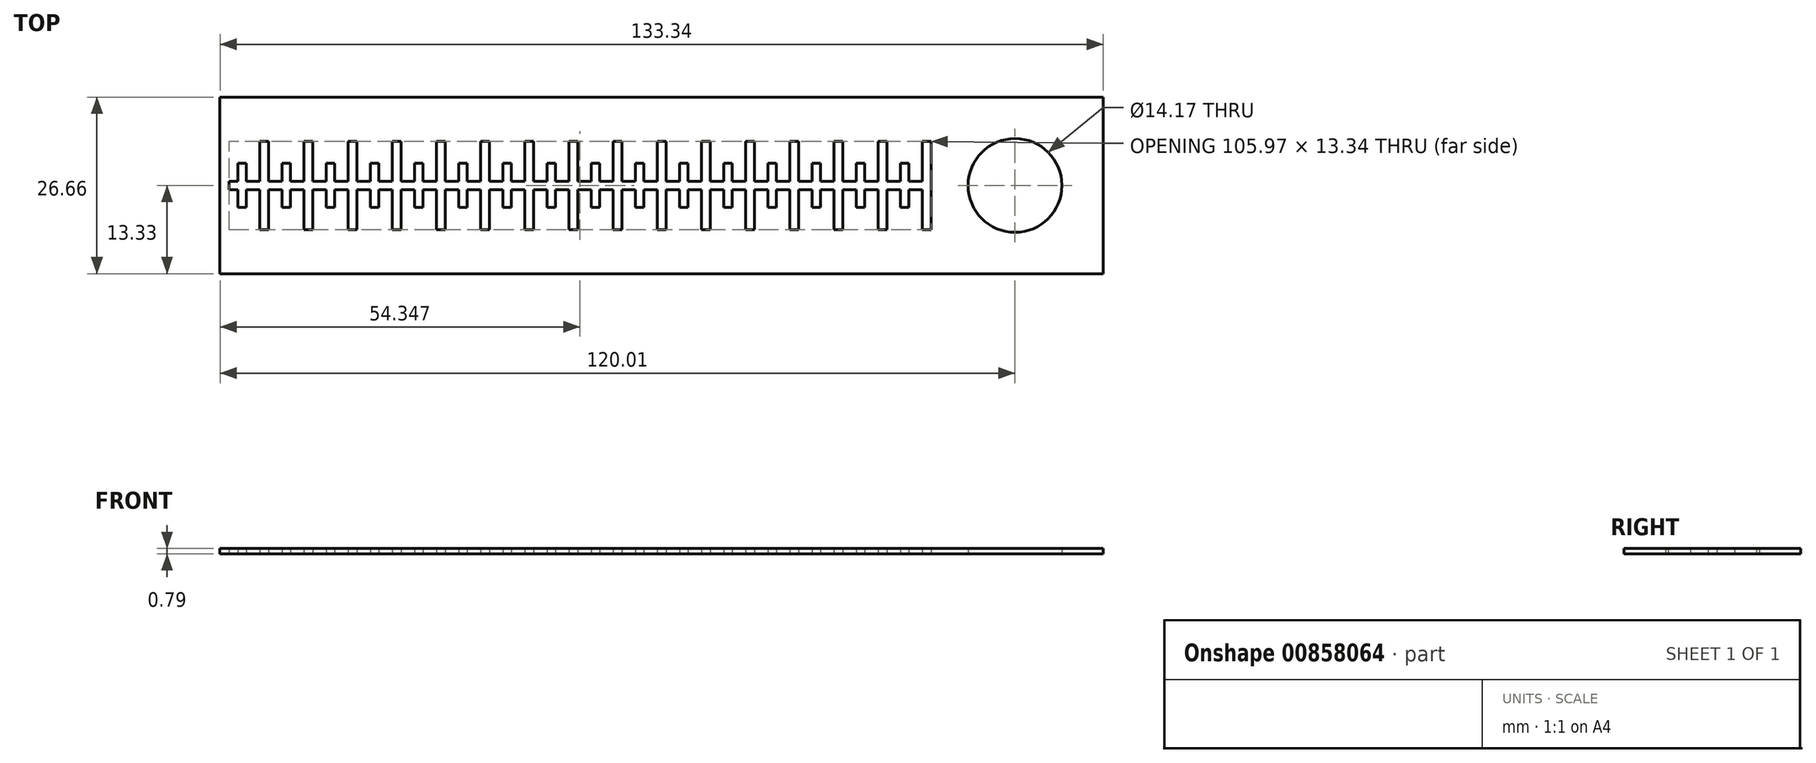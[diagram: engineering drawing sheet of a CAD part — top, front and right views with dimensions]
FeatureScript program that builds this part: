
annotation { "Feature Type Name" : "Feature", "Feature Type Description" : "" }
export const myFeature = defineFeature(function(context is Context, id is Id, definition is map)
    precondition{}
    {
        {
            var Q0;
            Q0=qCreatedBy(makeId("Top.planeOp"),FACE);
            var sketch = newSketch(context, id + "F0", { "sketchPlane" : qUnion([Q0])});
            skLineSegment(sketch, "E0.bottom", {"start": v(63.5, -12.7) * mm, "end": v(-63.5, -12.7) * mm});
            skLineSegment(sketch, "E0.top", {"start": v(63.5, 12.7) * mm, "end": v(-63.5, 12.7) * mm});
            skLineSegment(sketch, "E0.left", {"start": v(63.5, -12.7) * mm, "end": v(63.5, 12.7) * mm});
            skLineSegment(sketch, "E0.right", {"start": v(-63.5, -12.7) * mm, "end": v(-63.5, 12.7) * mm});
            skPoint(sketch, "E1", {"position": v(-60.33, 0) * mm});
            skPoint(sketch, "E2", {"position": v(-57.15, 0) * mm});
            skLineSegment(sketch, "E3.bottom", {"start": v(-57.15, -0.62) * mm, "end": v(-63.5, -0.62) * mm});
            skLineSegment(sketch, "E3.top", {"start": v(-57.15, 0.62) * mm, "end": v(-63.5, 0.62) * mm});
            skLineSegment(sketch, "E3.left", {"start": v(-57.15, -0.62) * mm, "end": v(-57.15, 0.62) * mm});
            skLineSegment(sketch, "E3.right", {"start": v(-63.5, -0.62) * mm, "end": v(-63.5, 0.62) * mm});
            skLineSegment(sketch, "E4.bottom", {"start": v(-59.7, -3.18) * mm, "end": v(-60.95, -3.18) * mm});
            skLineSegment(sketch, "E4.top", {"start": v(-59.7, 3.17) * mm, "end": v(-60.95, 3.17) * mm});
            skLineSegment(sketch, "E4.left", {"start": v(-59.7, -3.18) * mm, "end": v(-59.7, 3.17) * mm});
            skLineSegment(sketch, "E4.right", {"start": v(-60.95, -3.18) * mm, "end": v(-60.95, 3.17) * mm});
            skLineSegment(sketch, "E5.bottom", {"start": v(-56.52, -6.35) * mm, "end": v(-57.77, -6.35) * mm});
            skLineSegment(sketch, "E5.top", {"start": v(-56.52, 6.35) * mm, "end": v(-57.77, 6.35) * mm});
            skLineSegment(sketch, "E5.left", {"start": v(-56.52, -6.35) * mm, "end": v(-56.52, 6.35) * mm});
            skLineSegment(sketch, "E5.right", {"start": v(-57.77, -6.35) * mm, "end": v(-57.77, 6.35) * mm});
            skPoint(sketch, "E6.1.0.0", {"position": v(-50.8, 0) * mm});
            skLineSegment(sketch, "E6.1.0.1", {"start": v(-54.6, -3.18) * mm, "end": v(-54.6, 3.17) * mm});
            skLineSegment(sketch, "E6.1.0.2", {"start": v(-50.17, -6.35) * mm, "end": v(-50.17, 6.35) * mm});
            skPoint(sketch, "E6.1.0.3", {"position": v(-53.98, 0) * mm});
            skLineSegment(sketch, "E6.1.0.4", {"start": v(-53.35, -3.18) * mm, "end": v(-53.35, 3.17) * mm});
            skLineSegment(sketch, "E6.1.0.5", {"start": v(-51.42, -6.35) * mm, "end": v(-51.42, 6.35) * mm});
            skLineSegment(sketch, "E6.1.0.6", {"start": v(-50.8, 0.62) * mm, "end": v(-57.15, 0.62) * mm});
            skLineSegment(sketch, "E6.1.0.7", {"start": v(-50.8, -0.62) * mm, "end": v(-57.15, -0.62) * mm});
            skPoint(sketch, "E6.1.0.8", {"position": v(-50.8, 0) * mm});
            skPoint(sketch, "E6.1.0.9", {"position": v(-53.98, 0) * mm});
            skLineSegment(sketch, "E6.1.0.11", {"start": v(-50.8, -0.62) * mm, "end": v(-50.8, 0.62) * mm});
            skLineSegment(sketch, "E6.1.0.12", {"start": v(-53.35, -3.18) * mm, "end": v(-54.6, -3.18) * mm});
            skLineSegment(sketch, "E6.1.0.13", {"start": v(-53.35, 3.17) * mm, "end": v(-54.6, 3.17) * mm});
            skLineSegment(sketch, "E6.1.0.14", {"start": v(-50.17, -6.35) * mm, "end": v(-51.42, -6.35) * mm});
            skLineSegment(sketch, "E6.1.0.15", {"start": v(-50.17, 6.35) * mm, "end": v(-51.42, 6.35) * mm});
            skPoint(sketch, "E6.1.0.16", {"position": v(-53.98, 0) * mm});
            skPoint(sketch, "E6.2.0.0", {"position": v(-44.45, 0) * mm});
            skLineSegment(sketch, "E6.2.0.1", {"start": v(-48.25, -3.18) * mm, "end": v(-48.25, 3.17) * mm});
            skLineSegment(sketch, "E6.2.0.2", {"start": v(-43.82, -6.35) * mm, "end": v(-43.82, 6.35) * mm});
            skPoint(sketch, "E6.2.0.3", {"position": v(-47.62, 0) * mm});
            skLineSegment(sketch, "E6.2.0.4", {"start": v(-47, -3.18) * mm, "end": v(-47, 3.17) * mm});
            skLineSegment(sketch, "E6.2.0.5", {"start": v(-45.07, -6.35) * mm, "end": v(-45.07, 6.35) * mm});
            skLineSegment(sketch, "E6.2.0.6", {"start": v(-44.45, 0.62) * mm, "end": v(-50.8, 0.62) * mm});
            skLineSegment(sketch, "E6.2.0.7", {"start": v(-44.45, -0.62) * mm, "end": v(-50.8, -0.62) * mm});
            skPoint(sketch, "E6.2.0.8", {"position": v(-44.45, 0) * mm});
            skPoint(sketch, "E6.2.0.9", {"position": v(-47.62, 0) * mm});
            skLineSegment(sketch, "E6.2.0.10", {"start": v(-50.8, -0.62) * mm, "end": v(-50.8, 0.62) * mm});
            skLineSegment(sketch, "E6.2.0.11", {"start": v(-44.45, -0.62) * mm, "end": v(-44.45, 0.62) * mm});
            skLineSegment(sketch, "E6.2.0.12", {"start": v(-47, -3.18) * mm, "end": v(-48.25, -3.18) * mm});
            skLineSegment(sketch, "E6.2.0.13", {"start": v(-47, 3.17) * mm, "end": v(-48.25, 3.17) * mm});
            skLineSegment(sketch, "E6.2.0.14", {"start": v(-43.82, -6.35) * mm, "end": v(-45.07, -6.35) * mm});
            skLineSegment(sketch, "E6.2.0.15", {"start": v(-43.82, 6.35) * mm, "end": v(-45.07, 6.35) * mm});
            skPoint(sketch, "E6.2.0.16", {"position": v(-47.62, 0) * mm});
            skPoint(sketch, "E6.3.0.0", {"position": v(-38.1, 0) * mm});
            skLineSegment(sketch, "E6.3.0.1", {"start": v(-41.9, -3.18) * mm, "end": v(-41.9, 3.17) * mm});
            skLineSegment(sketch, "E6.3.0.2", {"start": v(-37.47, -6.35) * mm, "end": v(-37.47, 6.35) * mm});
            skPoint(sketch, "E6.3.0.3", {"position": v(-41.27, 0) * mm});
            skLineSegment(sketch, "E6.3.0.4", {"start": v(-40.65, -3.18) * mm, "end": v(-40.65, 3.17) * mm});
            skLineSegment(sketch, "E6.3.0.5", {"start": v(-38.72, -6.35) * mm, "end": v(-38.72, 6.35) * mm});
            skLineSegment(sketch, "E6.3.0.6", {"start": v(-38.1, 0.62) * mm, "end": v(-44.45, 0.62) * mm});
            skLineSegment(sketch, "E6.3.0.7", {"start": v(-38.1, -0.62) * mm, "end": v(-44.45, -0.62) * mm});
            skPoint(sketch, "E6.3.0.8", {"position": v(-38.1, 0) * mm});
            skPoint(sketch, "E6.3.0.9", {"position": v(-41.27, 0) * mm});
            skLineSegment(sketch, "E6.3.0.10", {"start": v(-44.45, -0.62) * mm, "end": v(-44.45, 0.62) * mm});
            skLineSegment(sketch, "E6.3.0.11", {"start": v(-38.1, -0.62) * mm, "end": v(-38.1, 0.62) * mm});
            skLineSegment(sketch, "E6.3.0.12", {"start": v(-40.65, -3.18) * mm, "end": v(-41.9, -3.18) * mm});
            skLineSegment(sketch, "E6.3.0.13", {"start": v(-40.65, 3.17) * mm, "end": v(-41.9, 3.17) * mm});
            skLineSegment(sketch, "E6.3.0.14", {"start": v(-37.47, -6.35) * mm, "end": v(-38.72, -6.35) * mm});
            skLineSegment(sketch, "E6.3.0.15", {"start": v(-37.47, 6.35) * mm, "end": v(-38.72, 6.35) * mm});
            skPoint(sketch, "E6.3.0.16", {"position": v(-41.27, 0) * mm});
            skPoint(sketch, "E6.4.0.0", {"position": v(-31.75, 0) * mm});
            skLineSegment(sketch, "E6.4.0.1", {"start": v(-35.55, -3.18) * mm, "end": v(-35.55, 3.17) * mm});
            skLineSegment(sketch, "E6.4.0.2", {"start": v(-31.12, -6.35) * mm, "end": v(-31.12, 6.35) * mm});
            skPoint(sketch, "E6.4.0.3", {"position": v(-34.92, 0) * mm});
            skLineSegment(sketch, "E6.4.0.4", {"start": v(-34.3, -3.18) * mm, "end": v(-34.3, 3.17) * mm});
            skLineSegment(sketch, "E6.4.0.5", {"start": v(-32.37, -6.35) * mm, "end": v(-32.37, 6.35) * mm});
            skLineSegment(sketch, "E6.4.0.6", {"start": v(-31.75, 0.62) * mm, "end": v(-38.1, 0.62) * mm});
            skLineSegment(sketch, "E6.4.0.7", {"start": v(-31.75, -0.62) * mm, "end": v(-38.1, -0.62) * mm});
            skPoint(sketch, "E6.4.0.8", {"position": v(-31.75, 0) * mm});
            skPoint(sketch, "E6.4.0.9", {"position": v(-34.92, 0) * mm});
            skLineSegment(sketch, "E6.4.0.10", {"start": v(-38.1, -0.62) * mm, "end": v(-38.1, 0.62) * mm});
            skLineSegment(sketch, "E6.4.0.11", {"start": v(-31.75, -0.62) * mm, "end": v(-31.75, 0.62) * mm});
            skLineSegment(sketch, "E6.4.0.12", {"start": v(-34.3, -3.18) * mm, "end": v(-35.55, -3.18) * mm});
            skLineSegment(sketch, "E6.4.0.13", {"start": v(-34.3, 3.17) * mm, "end": v(-35.55, 3.17) * mm});
            skLineSegment(sketch, "E6.4.0.14", {"start": v(-31.12, -6.35) * mm, "end": v(-32.37, -6.35) * mm});
            skLineSegment(sketch, "E6.4.0.15", {"start": v(-31.12, 6.35) * mm, "end": v(-32.37, 6.35) * mm});
            skPoint(sketch, "E6.4.0.16", {"position": v(-34.92, 0) * mm});
            skPoint(sketch, "E6.5.0.0", {"position": v(-25.4, 0) * mm});
            skLineSegment(sketch, "E6.5.0.1", {"start": v(-29.2, -3.18) * mm, "end": v(-29.2, 3.17) * mm});
            skLineSegment(sketch, "E6.5.0.2", {"start": v(-24.77, -6.35) * mm, "end": v(-24.77, 6.35) * mm});
            skPoint(sketch, "E6.5.0.3", {"position": v(-28.57, 0) * mm});
            skLineSegment(sketch, "E6.5.0.4", {"start": v(-27.95, -3.18) * mm, "end": v(-27.95, 3.17) * mm});
            skLineSegment(sketch, "E6.5.0.5", {"start": v(-26.02, -6.35) * mm, "end": v(-26.02, 6.35) * mm});
            skLineSegment(sketch, "E6.5.0.6", {"start": v(-25.4, 0.62) * mm, "end": v(-31.75, 0.62) * mm});
            skLineSegment(sketch, "E6.5.0.7", {"start": v(-25.4, -0.62) * mm, "end": v(-31.75, -0.62) * mm});
            skPoint(sketch, "E6.5.0.8", {"position": v(-25.4, 0) * mm});
            skPoint(sketch, "E6.5.0.9", {"position": v(-28.57, 0) * mm});
            skLineSegment(sketch, "E6.5.0.10", {"start": v(-31.75, -0.62) * mm, "end": v(-31.75, 0.62) * mm});
            skLineSegment(sketch, "E6.5.0.11", {"start": v(-25.4, -0.62) * mm, "end": v(-25.4, 0.62) * mm});
            skLineSegment(sketch, "E6.5.0.12", {"start": v(-27.95, -3.18) * mm, "end": v(-29.2, -3.18) * mm});
            skLineSegment(sketch, "E6.5.0.13", {"start": v(-27.95, 3.17) * mm, "end": v(-29.2, 3.17) * mm});
            skLineSegment(sketch, "E6.5.0.14", {"start": v(-24.77, -6.35) * mm, "end": v(-26.02, -6.35) * mm});
            skLineSegment(sketch, "E6.5.0.15", {"start": v(-24.77, 6.35) * mm, "end": v(-26.02, 6.35) * mm});
            skPoint(sketch, "E6.5.0.16", {"position": v(-28.57, 0) * mm});
            skPoint(sketch, "E6.6.0.0", {"position": v(-19.05, 0) * mm});
            skLineSegment(sketch, "E6.6.0.1", {"start": v(-22.85, -3.18) * mm, "end": v(-22.85, 3.17) * mm});
            skLineSegment(sketch, "E6.6.0.2", {"start": v(-18.42, -6.35) * mm, "end": v(-18.42, 6.35) * mm});
            skPoint(sketch, "E6.6.0.3", {"position": v(-22.22, 0) * mm});
            skLineSegment(sketch, "E6.6.0.4", {"start": v(-21.6, -3.18) * mm, "end": v(-21.6, 3.17) * mm});
            skLineSegment(sketch, "E6.6.0.5", {"start": v(-19.67, -6.35) * mm, "end": v(-19.67, 6.35) * mm});
            skLineSegment(sketch, "E6.6.0.6", {"start": v(-19.05, 0.62) * mm, "end": v(-25.4, 0.62) * mm});
            skLineSegment(sketch, "E6.6.0.7", {"start": v(-19.05, -0.62) * mm, "end": v(-25.4, -0.62) * mm});
            skPoint(sketch, "E6.6.0.8", {"position": v(-19.05, 0) * mm});
            skPoint(sketch, "E6.6.0.9", {"position": v(-22.22, 0) * mm});
            skLineSegment(sketch, "E6.6.0.10", {"start": v(-25.4, -0.62) * mm, "end": v(-25.4, 0.62) * mm});
            skLineSegment(sketch, "E6.6.0.11", {"start": v(-19.05, -0.62) * mm, "end": v(-19.05, 0.62) * mm});
            skLineSegment(sketch, "E6.6.0.12", {"start": v(-21.6, -3.18) * mm, "end": v(-22.85, -3.18) * mm});
            skLineSegment(sketch, "E6.6.0.13", {"start": v(-21.6, 3.17) * mm, "end": v(-22.85, 3.17) * mm});
            skLineSegment(sketch, "E6.6.0.14", {"start": v(-18.42, -6.35) * mm, "end": v(-19.67, -6.35) * mm});
            skLineSegment(sketch, "E6.6.0.15", {"start": v(-18.42, 6.35) * mm, "end": v(-19.67, 6.35) * mm});
            skPoint(sketch, "E6.6.0.16", {"position": v(-22.22, 0) * mm});
            skPoint(sketch, "E6.7.0.0", {"position": v(-12.7, 0) * mm});
            skLineSegment(sketch, "E6.7.0.1", {"start": v(-16.5, -3.18) * mm, "end": v(-16.5, 3.17) * mm});
            skLineSegment(sketch, "E6.7.0.2", {"start": v(-12.07, -6.35) * mm, "end": v(-12.07, 6.35) * mm});
            skPoint(sketch, "E6.7.0.3", {"position": v(-15.87, 0) * mm});
            skLineSegment(sketch, "E6.7.0.4", {"start": v(-15.25, -3.18) * mm, "end": v(-15.25, 3.17) * mm});
            skLineSegment(sketch, "E6.7.0.5", {"start": v(-13.32, -6.35) * mm, "end": v(-13.32, 6.35) * mm});
            skLineSegment(sketch, "E6.7.0.6", {"start": v(-12.7, 0.62) * mm, "end": v(-19.05, 0.62) * mm});
            skLineSegment(sketch, "E6.7.0.7", {"start": v(-12.7, -0.62) * mm, "end": v(-19.05, -0.62) * mm});
            skPoint(sketch, "E6.7.0.8", {"position": v(-12.7, 0) * mm});
            skPoint(sketch, "E6.7.0.9", {"position": v(-15.87, 0) * mm});
            skLineSegment(sketch, "E6.7.0.10", {"start": v(-19.05, -0.62) * mm, "end": v(-19.05, 0.62) * mm});
            skLineSegment(sketch, "E6.7.0.11", {"start": v(-12.7, -0.62) * mm, "end": v(-12.7, 0.62) * mm});
            skLineSegment(sketch, "E6.7.0.12", {"start": v(-15.25, -3.18) * mm, "end": v(-16.5, -3.18) * mm});
            skLineSegment(sketch, "E6.7.0.13", {"start": v(-15.25, 3.17) * mm, "end": v(-16.5, 3.17) * mm});
            skLineSegment(sketch, "E6.7.0.14", {"start": v(-12.07, -6.35) * mm, "end": v(-13.32, -6.35) * mm});
            skLineSegment(sketch, "E6.7.0.15", {"start": v(-12.07, 6.35) * mm, "end": v(-13.32, 6.35) * mm});
            skPoint(sketch, "E6.7.0.16", {"position": v(-15.87, 0) * mm});
            skPoint(sketch, "E6.8.0.0", {"position": v(-6.35, 0) * mm});
            skLineSegment(sketch, "E6.8.0.1", {"start": v(-10.15, -3.18) * mm, "end": v(-10.15, 3.17) * mm});
            skLineSegment(sketch, "E6.8.0.2", {"start": v(-5.72, -6.35) * mm, "end": v(-5.72, 6.35) * mm});
            skPoint(sketch, "E6.8.0.3", {"position": v(-9.52, 0) * mm});
            skLineSegment(sketch, "E6.8.0.4", {"start": v(-8.9, -3.18) * mm, "end": v(-8.9, 3.17) * mm});
            skLineSegment(sketch, "E6.8.0.5", {"start": v(-6.97, -6.35) * mm, "end": v(-6.97, 6.35) * mm});
            skLineSegment(sketch, "E6.8.0.6", {"start": v(-6.35, 0.62) * mm, "end": v(-12.7, 0.62) * mm});
            skLineSegment(sketch, "E6.8.0.7", {"start": v(-6.35, -0.62) * mm, "end": v(-12.7, -0.62) * mm});
            skPoint(sketch, "E6.8.0.8", {"position": v(-6.35, 0) * mm});
            skPoint(sketch, "E6.8.0.9", {"position": v(-9.52, 0) * mm});
            skLineSegment(sketch, "E6.8.0.10", {"start": v(-12.7, -0.62) * mm, "end": v(-12.7, 0.62) * mm});
            skLineSegment(sketch, "E6.8.0.11", {"start": v(-6.35, -0.62) * mm, "end": v(-6.35, 0.62) * mm});
            skLineSegment(sketch, "E6.8.0.12", {"start": v(-8.9, -3.18) * mm, "end": v(-10.15, -3.18) * mm});
            skLineSegment(sketch, "E6.8.0.13", {"start": v(-8.9, 3.17) * mm, "end": v(-10.15, 3.17) * mm});
            skLineSegment(sketch, "E6.8.0.14", {"start": v(-5.72, -6.35) * mm, "end": v(-6.97, -6.35) * mm});
            skLineSegment(sketch, "E6.8.0.15", {"start": v(-5.72, 6.35) * mm, "end": v(-6.97, 6.35) * mm});
            skPoint(sketch, "E6.8.0.16", {"position": v(-9.52, 0) * mm});
            skPoint(sketch, "E6.9.0.0", {"position": v(0, 0) * mm});
            skLineSegment(sketch, "E6.9.0.1", {"start": v(-3.8, -3.18) * mm, "end": v(-3.8, 3.17) * mm});
            skLineSegment(sketch, "E6.9.0.2", {"start": v(0.63, -6.35) * mm, "end": v(0.63, 6.35) * mm});
            skPoint(sketch, "E6.9.0.3", {"position": v(-3.17, 0) * mm});
            skLineSegment(sketch, "E6.9.0.4", {"start": v(-2.55, -3.18) * mm, "end": v(-2.55, 3.17) * mm});
            skLineSegment(sketch, "E6.9.0.5", {"start": v(-0.62, -6.35) * mm, "end": v(-0.62, 6.35) * mm});
            skLineSegment(sketch, "E6.9.0.6", {"start": v(0, 0.62) * mm, "end": v(-6.35, 0.62) * mm});
            skLineSegment(sketch, "E6.9.0.7", {"start": v(0, -0.62) * mm, "end": v(-6.35, -0.62) * mm});
            skPoint(sketch, "E6.9.0.8", {"position": v(0, 0) * mm});
            skPoint(sketch, "E6.9.0.9", {"position": v(-3.17, 0) * mm});
            skLineSegment(sketch, "E6.9.0.10", {"start": v(-6.35, -0.62) * mm, "end": v(-6.35, 0.62) * mm});
            skLineSegment(sketch, "E6.9.0.11", {"start": v(0, -0.62) * mm, "end": v(0, 0.62) * mm});
            skLineSegment(sketch, "E6.9.0.12", {"start": v(-2.55, -3.18) * mm, "end": v(-3.8, -3.18) * mm});
            skLineSegment(sketch, "E6.9.0.13", {"start": v(-2.55, 3.17) * mm, "end": v(-3.8, 3.17) * mm});
            skLineSegment(sketch, "E6.9.0.14", {"start": v(0.63, -6.35) * mm, "end": v(-0.62, -6.35) * mm});
            skLineSegment(sketch, "E6.9.0.15", {"start": v(0.63, 6.35) * mm, "end": v(-0.62, 6.35) * mm});
            skPoint(sketch, "E6.9.0.16", {"position": v(-3.17, 0) * mm});
            skPoint(sketch, "E6.10.0.0", {"position": v(6.35, 0) * mm});
            skLineSegment(sketch, "E6.10.0.1", {"start": v(2.55, -3.18) * mm, "end": v(2.55, 3.17) * mm});
            skLineSegment(sketch, "E6.10.0.2", {"start": v(6.98, -6.35) * mm, "end": v(6.98, 6.35) * mm});
            skPoint(sketch, "E6.10.0.3", {"position": v(3.18, 0) * mm});
            skLineSegment(sketch, "E6.10.0.4", {"start": v(3.8, -3.18) * mm, "end": v(3.8, 3.17) * mm});
            skLineSegment(sketch, "E6.10.0.5", {"start": v(5.73, -6.35) * mm, "end": v(5.73, 6.35) * mm});
            skLineSegment(sketch, "E6.10.0.6", {"start": v(6.35, 0.62) * mm, "end": v(0, 0.62) * mm});
            skLineSegment(sketch, "E6.10.0.7", {"start": v(6.35, -0.62) * mm, "end": v(0, -0.62) * mm});
            skPoint(sketch, "E6.10.0.8", {"position": v(6.35, 0) * mm});
            skPoint(sketch, "E6.10.0.9", {"position": v(3.18, 0) * mm});
            skLineSegment(sketch, "E6.10.0.10", {"start": v(0, -0.62) * mm, "end": v(0, 0.62) * mm});
            skLineSegment(sketch, "E6.10.0.11", {"start": v(6.35, -0.62) * mm, "end": v(6.35, 0.62) * mm});
            skLineSegment(sketch, "E6.10.0.12", {"start": v(3.8, -3.18) * mm, "end": v(2.55, -3.18) * mm});
            skLineSegment(sketch, "E6.10.0.13", {"start": v(3.8, 3.17) * mm, "end": v(2.55, 3.17) * mm});
            skLineSegment(sketch, "E6.10.0.14", {"start": v(6.98, -6.35) * mm, "end": v(5.73, -6.35) * mm});
            skLineSegment(sketch, "E6.10.0.15", {"start": v(6.98, 6.35) * mm, "end": v(5.73, 6.35) * mm});
            skPoint(sketch, "E6.10.0.16", {"position": v(3.18, 0) * mm});
            skPoint(sketch, "E6.11.0.0", {"position": v(12.7, 0) * mm});
            skLineSegment(sketch, "E6.11.0.1", {"start": v(8.9, -3.18) * mm, "end": v(8.9, 3.17) * mm});
            skLineSegment(sketch, "E6.11.0.2", {"start": v(13.33, -6.35) * mm, "end": v(13.33, 6.35) * mm});
            skPoint(sketch, "E6.11.0.3", {"position": v(9.53, 0) * mm});
            skLineSegment(sketch, "E6.11.0.4", {"start": v(10.15, -3.18) * mm, "end": v(10.15, 3.17) * mm});
            skLineSegment(sketch, "E6.11.0.5", {"start": v(12.08, -6.35) * mm, "end": v(12.08, 6.35) * mm});
            skLineSegment(sketch, "E6.11.0.6", {"start": v(12.7, 0.62) * mm, "end": v(6.35, 0.62) * mm});
            skLineSegment(sketch, "E6.11.0.7", {"start": v(12.7, -0.62) * mm, "end": v(6.35, -0.62) * mm});
            skPoint(sketch, "E6.11.0.8", {"position": v(12.7, 0) * mm});
            skPoint(sketch, "E6.11.0.9", {"position": v(9.53, 0) * mm});
            skLineSegment(sketch, "E6.11.0.10", {"start": v(6.35, -0.62) * mm, "end": v(6.35, 0.62) * mm});
            skLineSegment(sketch, "E6.11.0.11", {"start": v(12.7, -0.62) * mm, "end": v(12.7, 0.62) * mm});
            skLineSegment(sketch, "E6.11.0.12", {"start": v(10.15, -3.18) * mm, "end": v(8.9, -3.18) * mm});
            skLineSegment(sketch, "E6.11.0.13", {"start": v(10.15, 3.17) * mm, "end": v(8.9, 3.17) * mm});
            skLineSegment(sketch, "E6.11.0.14", {"start": v(13.33, -6.35) * mm, "end": v(12.08, -6.35) * mm});
            skLineSegment(sketch, "E6.11.0.15", {"start": v(13.33, 6.35) * mm, "end": v(12.08, 6.35) * mm});
            skPoint(sketch, "E6.11.0.16", {"position": v(9.53, 0) * mm});
            skPoint(sketch, "E6.12.0.0", {"position": v(19.05, 0) * mm});
            skLineSegment(sketch, "E6.12.0.1", {"start": v(15.25, -3.18) * mm, "end": v(15.25, 3.17) * mm});
            skLineSegment(sketch, "E6.12.0.2", {"start": v(19.68, -6.35) * mm, "end": v(19.68, 6.35) * mm});
            skPoint(sketch, "E6.12.0.3", {"position": v(15.88, 0) * mm});
            skLineSegment(sketch, "E6.12.0.4", {"start": v(16.5, -3.18) * mm, "end": v(16.5, 3.17) * mm});
            skLineSegment(sketch, "E6.12.0.5", {"start": v(18.43, -6.35) * mm, "end": v(18.43, 6.35) * mm});
            skLineSegment(sketch, "E6.12.0.6", {"start": v(19.05, 0.62) * mm, "end": v(12.7, 0.62) * mm});
            skLineSegment(sketch, "E6.12.0.7", {"start": v(19.05, -0.62) * mm, "end": v(12.7, -0.62) * mm});
            skPoint(sketch, "E6.12.0.8", {"position": v(19.05, 0) * mm});
            skPoint(sketch, "E6.12.0.9", {"position": v(15.88, 0) * mm});
            skLineSegment(sketch, "E6.12.0.10", {"start": v(12.7, -0.62) * mm, "end": v(12.7, 0.62) * mm});
            skLineSegment(sketch, "E6.12.0.11", {"start": v(19.05, -0.62) * mm, "end": v(19.05, 0.62) * mm});
            skLineSegment(sketch, "E6.12.0.12", {"start": v(16.5, -3.18) * mm, "end": v(15.25, -3.18) * mm});
            skLineSegment(sketch, "E6.12.0.13", {"start": v(16.5, 3.17) * mm, "end": v(15.25, 3.17) * mm});
            skLineSegment(sketch, "E6.12.0.14", {"start": v(19.68, -6.35) * mm, "end": v(18.43, -6.35) * mm});
            skLineSegment(sketch, "E6.12.0.15", {"start": v(19.68, 6.35) * mm, "end": v(18.43, 6.35) * mm});
            skPoint(sketch, "E6.12.0.16", {"position": v(15.88, 0) * mm});
            skPoint(sketch, "E6.13.0.0", {"position": v(25.4, 0) * mm});
            skLineSegment(sketch, "E6.13.0.1", {"start": v(21.6, -3.18) * mm, "end": v(21.6, 3.17) * mm});
            skLineSegment(sketch, "E6.13.0.2", {"start": v(26.03, -6.35) * mm, "end": v(26.03, 6.35) * mm});
            skPoint(sketch, "E6.13.0.3", {"position": v(22.23, 0) * mm});
            skLineSegment(sketch, "E6.13.0.4", {"start": v(22.85, -3.18) * mm, "end": v(22.85, 3.17) * mm});
            skLineSegment(sketch, "E6.13.0.5", {"start": v(24.78, -6.35) * mm, "end": v(24.78, 6.35) * mm});
            skLineSegment(sketch, "E6.13.0.6", {"start": v(25.4, 0.62) * mm, "end": v(19.05, 0.62) * mm});
            skLineSegment(sketch, "E6.13.0.7", {"start": v(25.4, -0.62) * mm, "end": v(19.05, -0.62) * mm});
            skPoint(sketch, "E6.13.0.8", {"position": v(25.4, 0) * mm});
            skPoint(sketch, "E6.13.0.9", {"position": v(22.23, 0) * mm});
            skLineSegment(sketch, "E6.13.0.10", {"start": v(19.05, -0.62) * mm, "end": v(19.05, 0.62) * mm});
            skLineSegment(sketch, "E6.13.0.11", {"start": v(25.4, -0.62) * mm, "end": v(25.4, 0.62) * mm});
            skLineSegment(sketch, "E6.13.0.12", {"start": v(22.85, -3.18) * mm, "end": v(21.6, -3.18) * mm});
            skLineSegment(sketch, "E6.13.0.13", {"start": v(22.85, 3.17) * mm, "end": v(21.6, 3.17) * mm});
            skLineSegment(sketch, "E6.13.0.14", {"start": v(26.03, -6.35) * mm, "end": v(24.78, -6.35) * mm});
            skLineSegment(sketch, "E6.13.0.15", {"start": v(26.03, 6.35) * mm, "end": v(24.78, 6.35) * mm});
            skPoint(sketch, "E6.13.0.16", {"position": v(22.23, 0) * mm});
            skLineSegment(sketch, "E6.direction1", {"start": v(-57.77, -6.35) * mm, "end": v(-51.42, -6.35) * mm, "construction": true});
            skPoint(sketch, "E7.0.14.0", {"position": v(31.75, 0) * mm});
            skLineSegment(sketch, "E7.1.14.0", {"start": v(27.95, -3.18) * mm, "end": v(27.95, 3.17) * mm});
            skLineSegment(sketch, "E7.4.14.0", {"start": v(32.38, -6.35) * mm, "end": v(32.38, 6.35) * mm});
            skPoint(sketch, "E7.7.14.0", {"position": v(28.58, 0) * mm});
            skLineSegment(sketch, "E7.8.14.0", {"start": v(29.2, -3.18) * mm, "end": v(29.2, 3.17) * mm});
            skLineSegment(sketch, "E7.11.14.0", {"start": v(31.13, -6.35) * mm, "end": v(31.13, 6.35) * mm});
            skLineSegment(sketch, "E7.14.14.0", {"start": v(31.75, 0.62) * mm, "end": v(25.4, 0.62) * mm});
            skLineSegment(sketch, "E7.17.14.0", {"start": v(31.75, -0.62) * mm, "end": v(25.4, -0.62) * mm});
            skPoint(sketch, "E7.20.14.0", {"position": v(31.75, 0) * mm});
            skPoint(sketch, "E7.21.14.0", {"position": v(28.58, 0) * mm});
            skLineSegment(sketch, "E7.25.14.0", {"start": v(31.75, -0.62) * mm, "end": v(31.75, 0.62) * mm});
            skLineSegment(sketch, "E7.28.14.0", {"start": v(29.2, -3.18) * mm, "end": v(27.95, -3.18) * mm});
            skLineSegment(sketch, "E7.31.14.0", {"start": v(29.2, 3.17) * mm, "end": v(27.95, 3.17) * mm});
            skLineSegment(sketch, "E7.34.14.0", {"start": v(32.38, -6.35) * mm, "end": v(31.13, -6.35) * mm});
            skLineSegment(sketch, "E7.37.14.0", {"start": v(32.38, 6.35) * mm, "end": v(31.13, 6.35) * mm});
            skPoint(sketch, "E7.40.14.0", {"position": v(28.58, 0) * mm});
            skPoint(sketch, "E7.0.15.0", {"position": v(38.1, 0) * mm});
            skLineSegment(sketch, "E7.1.15.0", {"start": v(34.3, -3.18) * mm, "end": v(34.3, 3.17) * mm});
            skLineSegment(sketch, "E7.4.15.0", {"start": v(38.73, -6.35) * mm, "end": v(38.73, 6.35) * mm});
            skPoint(sketch, "E7.7.15.0", {"position": v(34.93, 0) * mm});
            skLineSegment(sketch, "E7.8.15.0", {"start": v(35.55, -3.18) * mm, "end": v(35.55, 3.17) * mm});
            skLineSegment(sketch, "E7.11.15.0", {"start": v(37.48, -6.35) * mm, "end": v(37.48, 6.35) * mm});
            skLineSegment(sketch, "E7.14.15.0", {"start": v(38.1, 0.62) * mm, "end": v(31.75, 0.62) * mm});
            skLineSegment(sketch, "E7.17.15.0", {"start": v(38.1, -0.62) * mm, "end": v(31.75, -0.62) * mm});
            skPoint(sketch, "E7.20.15.0", {"position": v(38.1, 0) * mm});
            skPoint(sketch, "E7.21.15.0", {"position": v(34.93, 0) * mm});
            skLineSegment(sketch, "E7.22.15.0", {"start": v(31.75, -0.62) * mm, "end": v(31.75, 0.62) * mm});
            skLineSegment(sketch, "E7.25.15.0", {"start": v(38.1, -0.62) * mm, "end": v(38.1, 0.62) * mm});
            skLineSegment(sketch, "E7.28.15.0", {"start": v(35.55, -3.18) * mm, "end": v(34.3, -3.18) * mm});
            skLineSegment(sketch, "E7.31.15.0", {"start": v(35.55, 3.17) * mm, "end": v(34.3, 3.17) * mm});
            skLineSegment(sketch, "E7.34.15.0", {"start": v(38.73, -6.35) * mm, "end": v(37.48, -6.35) * mm});
            skLineSegment(sketch, "E7.37.15.0", {"start": v(38.73, 6.35) * mm, "end": v(37.48, 6.35) * mm});
            skPoint(sketch, "E7.40.15.0", {"position": v(34.93, 0) * mm});
            skPoint(sketch, "E8.positionSnap0", {"position": v(35.55, 0) * mm});
            skPoint(sketch, "E9", {"position": v(63.5, 0) * mm});
            skPoint(sketch, "E10", {"position": v(50.8, 0) * mm});
            skLineSegment(sketch, "E11.left", {"start": v(-63.5, 1.74) * mm, "end": v(-63.5, -1.65) * mm});
            skLineSegment(sketch, "E12", {"start": v(-62.2, 0.62) * mm, "end": v(-62.2, -0.62) * mm});
            skSolve(sketch);
        }
        {
            var Q0;
            {var subQ174=sQuery(id+"F0.wireOp",EDGE,"E0.bottom");Q0=makeQuery(id+"F0.imprint","IMPRINT",FACE,{"disambiguationData":[TD([[makeQuery(id+"F0.imprint","IMPRINT",EDGE,{"derivedFrom":subQ174}),-1.0]])]});}
            extrude(context, id + "F1", {"entities" : qUnion([Q0]), "depth" : .75 * mm, "offsetDistance" : 25 * mm});
        }
        {
            var Q0;
            Q0=sQuery(id+"F0.wireOp",VERTEX,"E10");
            var Q1;
            Q1=makeQuery(id+"F1.opExtrude","SWEPT_BODY",BODY,{"disambiguationData":[OSD([sQuery(id+"F0.wireOp",EDGE,"E0.bottom"),sQuery(id+"F0.wireOp",EDGE,"E0.top"),sQuery(id+"F0.wireOp",EDGE,"E0.left"),sQuery(id+"F0.wireOp",EDGE,"E0.right"),sQuery(id+"F0.wireOp",EDGE,"E3.bottom"),sQuery(id+"F0.wireOp",EDGE,"E3.top"),sQuery(id+"F0.wireOp",EDGE,"E4.bottom"),sQuery(id+"F0.wireOp",EDGE,"E4.top"),sQuery(id+"F0.wireOp",EDGE,"E4.left"),sQuery(id+"F0.wireOp",EDGE,"E4.right"),sQuery(id+"F0.wireOp",EDGE,"E5.bottom"),sQuery(id+"F0.wireOp",EDGE,"E5.top"),sQuery(id+"F0.wireOp",EDGE,"E5.left"),sQuery(id+"F0.wireOp",EDGE,"E5.right"),sQuery(id+"F0.wireOp",EDGE,"E6.1.0.1"),sQuery(id+"F0.wireOp",EDGE,"E6.1.0.2"),sQuery(id+"F0.wireOp",EDGE,"E6.1.0.4"),sQuery(id+"F0.wireOp",EDGE,"E6.1.0.5"),sQuery(id+"F0.wireOp",EDGE,"E6.1.0.6"),sQuery(id+"F0.wireOp",EDGE,"E6.1.0.7"),sQuery(id+"F0.wireOp",EDGE,"E6.1.0.12"),sQuery(id+"F0.wireOp",EDGE,"E6.1.0.13"),sQuery(id+"F0.wireOp",EDGE,"E6.1.0.14"),sQuery(id+"F0.wireOp",EDGE,"E6.1.0.15"),sQuery(id+"F0.wireOp",EDGE,"E6.2.0.1"),sQuery(id+"F0.wireOp",EDGE,"E6.2.0.2"),sQuery(id+"F0.wireOp",EDGE,"E6.2.0.4"),sQuery(id+"F0.wireOp",EDGE,"E6.2.0.5"),sQuery(id+"F0.wireOp",EDGE,"E6.2.0.6"),sQuery(id+"F0.wireOp",EDGE,"E6.2.0.7"),sQuery(id+"F0.wireOp",EDGE,"E6.2.0.12"),sQuery(id+"F0.wireOp",EDGE,"E6.2.0.13"),sQuery(id+"F0.wireOp",EDGE,"E6.2.0.14"),sQuery(id+"F0.wireOp",EDGE,"E6.2.0.15"),sQuery(id+"F0.wireOp",EDGE,"E6.3.0.1"),sQuery(id+"F0.wireOp",EDGE,"E6.3.0.2"),sQuery(id+"F0.wireOp",EDGE,"E6.3.0.4"),sQuery(id+"F0.wireOp",EDGE,"E6.3.0.5"),sQuery(id+"F0.wireOp",EDGE,"E6.3.0.6"),sQuery(id+"F0.wireOp",EDGE,"E6.3.0.7"),sQuery(id+"F0.wireOp",EDGE,"E6.3.0.12"),sQuery(id+"F0.wireOp",EDGE,"E6.3.0.13"),sQuery(id+"F0.wireOp",EDGE,"E6.3.0.14"),sQuery(id+"F0.wireOp",EDGE,"E6.3.0.15"),sQuery(id+"F0.wireOp",EDGE,"E6.4.0.1"),sQuery(id+"F0.wireOp",EDGE,"E6.4.0.2"),sQuery(id+"F0.wireOp",EDGE,"E6.4.0.4"),sQuery(id+"F0.wireOp",EDGE,"E6.4.0.5"),sQuery(id+"F0.wireOp",EDGE,"E6.4.0.6"),sQuery(id+"F0.wireOp",EDGE,"E6.4.0.7"),sQuery(id+"F0.wireOp",EDGE,"E6.4.0.12"),sQuery(id+"F0.wireOp",EDGE,"E6.4.0.13"),sQuery(id+"F0.wireOp",EDGE,"E6.4.0.14"),sQuery(id+"F0.wireOp",EDGE,"E6.4.0.15"),sQuery(id+"F0.wireOp",EDGE,"E6.5.0.1"),sQuery(id+"F0.wireOp",EDGE,"E6.5.0.2"),sQuery(id+"F0.wireOp",EDGE,"E6.5.0.4"),sQuery(id+"F0.wireOp",EDGE,"E6.5.0.5"),sQuery(id+"F0.wireOp",EDGE,"E6.5.0.6"),sQuery(id+"F0.wireOp",EDGE,"E6.5.0.7"),sQuery(id+"F0.wireOp",EDGE,"E6.5.0.12"),sQuery(id+"F0.wireOp",EDGE,"E6.5.0.13"),sQuery(id+"F0.wireOp",EDGE,"E6.5.0.14"),sQuery(id+"F0.wireOp",EDGE,"E6.5.0.15"),sQuery(id+"F0.wireOp",EDGE,"E6.6.0.1"),sQuery(id+"F0.wireOp",EDGE,"E6.6.0.2"),sQuery(id+"F0.wireOp",EDGE,"E6.6.0.4"),sQuery(id+"F0.wireOp",EDGE,"E6.6.0.5"),sQuery(id+"F0.wireOp",EDGE,"E6.6.0.6"),sQuery(id+"F0.wireOp",EDGE,"E6.6.0.7"),sQuery(id+"F0.wireOp",EDGE,"E6.6.0.12"),sQuery(id+"F0.wireOp",EDGE,"E6.6.0.13"),sQuery(id+"F0.wireOp",EDGE,"E6.6.0.14"),sQuery(id+"F0.wireOp",EDGE,"E6.6.0.15"),sQuery(id+"F0.wireOp",EDGE,"E6.7.0.1"),sQuery(id+"F0.wireOp",EDGE,"E6.7.0.2"),sQuery(id+"F0.wireOp",EDGE,"E6.7.0.4"),sQuery(id+"F0.wireOp",EDGE,"E6.7.0.5"),sQuery(id+"F0.wireOp",EDGE,"E6.7.0.6"),sQuery(id+"F0.wireOp",EDGE,"E6.7.0.7"),sQuery(id+"F0.wireOp",EDGE,"E6.7.0.12"),sQuery(id+"F0.wireOp",EDGE,"E6.7.0.13"),sQuery(id+"F0.wireOp",EDGE,"E6.7.0.14"),sQuery(id+"F0.wireOp",EDGE,"E6.7.0.15"),sQuery(id+"F0.wireOp",EDGE,"E6.8.0.1"),sQuery(id+"F0.wireOp",EDGE,"E6.8.0.2"),sQuery(id+"F0.wireOp",EDGE,"E6.8.0.4"),sQuery(id+"F0.wireOp",EDGE,"E6.8.0.5"),sQuery(id+"F0.wireOp",EDGE,"E6.8.0.6"),sQuery(id+"F0.wireOp",EDGE,"E6.8.0.7"),sQuery(id+"F0.wireOp",EDGE,"E6.8.0.12"),sQuery(id+"F0.wireOp",EDGE,"E6.8.0.13"),sQuery(id+"F0.wireOp",EDGE,"E6.8.0.14"),sQuery(id+"F0.wireOp",EDGE,"E6.8.0.15"),sQuery(id+"F0.wireOp",EDGE,"E6.9.0.1"),sQuery(id+"F0.wireOp",EDGE,"E6.9.0.2"),sQuery(id+"F0.wireOp",EDGE,"E6.9.0.4"),sQuery(id+"F0.wireOp",EDGE,"E6.9.0.5"),sQuery(id+"F0.wireOp",EDGE,"E6.9.0.6"),sQuery(id+"F0.wireOp",EDGE,"E6.9.0.7"),sQuery(id+"F0.wireOp",EDGE,"E6.9.0.12"),sQuery(id+"F0.wireOp",EDGE,"E6.9.0.13"),sQuery(id+"F0.wireOp",EDGE,"E6.9.0.14"),sQuery(id+"F0.wireOp",EDGE,"E6.9.0.15"),sQuery(id+"F0.wireOp",EDGE,"E6.10.0.1"),sQuery(id+"F0.wireOp",EDGE,"E6.10.0.2"),sQuery(id+"F0.wireOp",EDGE,"E6.10.0.4"),sQuery(id+"F0.wireOp",EDGE,"E6.10.0.5"),sQuery(id+"F0.wireOp",EDGE,"E6.10.0.6"),sQuery(id+"F0.wireOp",EDGE,"E6.10.0.7"),sQuery(id+"F0.wireOp",EDGE,"E6.10.0.12"),sQuery(id+"F0.wireOp",EDGE,"E6.10.0.13"),sQuery(id+"F0.wireOp",EDGE,"E6.10.0.14"),sQuery(id+"F0.wireOp",EDGE,"E6.10.0.15"),sQuery(id+"F0.wireOp",EDGE,"E6.11.0.1"),sQuery(id+"F0.wireOp",EDGE,"E6.11.0.2"),sQuery(id+"F0.wireOp",EDGE,"E6.11.0.4"),sQuery(id+"F0.wireOp",EDGE,"E6.11.0.5"),sQuery(id+"F0.wireOp",EDGE,"E6.11.0.6"),sQuery(id+"F0.wireOp",EDGE,"E6.11.0.7"),sQuery(id+"F0.wireOp",EDGE,"E6.11.0.12"),sQuery(id+"F0.wireOp",EDGE,"E6.11.0.13"),sQuery(id+"F0.wireOp",EDGE,"E6.11.0.14"),sQuery(id+"F0.wireOp",EDGE,"E6.11.0.15"),sQuery(id+"F0.wireOp",EDGE,"E6.12.0.1"),sQuery(id+"F0.wireOp",EDGE,"E6.12.0.2"),sQuery(id+"F0.wireOp",EDGE,"E6.12.0.4"),sQuery(id+"F0.wireOp",EDGE,"E6.12.0.5"),sQuery(id+"F0.wireOp",EDGE,"E6.12.0.6"),sQuery(id+"F0.wireOp",EDGE,"E6.12.0.7"),sQuery(id+"F0.wireOp",EDGE,"E6.12.0.12"),sQuery(id+"F0.wireOp",EDGE,"E6.12.0.13"),sQuery(id+"F0.wireOp",EDGE,"E6.12.0.14"),sQuery(id+"F0.wireOp",EDGE,"E6.12.0.15"),sQuery(id+"F0.wireOp",EDGE,"E6.13.0.1"),sQuery(id+"F0.wireOp",EDGE,"E6.13.0.2"),sQuery(id+"F0.wireOp",EDGE,"E6.13.0.4"),sQuery(id+"F0.wireOp",EDGE,"E6.13.0.5"),sQuery(id+"F0.wireOp",EDGE,"E6.13.0.6"),sQuery(id+"F0.wireOp",EDGE,"E6.13.0.7"),sQuery(id+"F0.wireOp",EDGE,"E6.13.0.12"),sQuery(id+"F0.wireOp",EDGE,"E6.13.0.13"),sQuery(id+"F0.wireOp",EDGE,"E6.13.0.14"),sQuery(id+"F0.wireOp",EDGE,"E6.13.0.15"),sQuery(id+"F0.wireOp",EDGE,"E7.1.14.0"),sQuery(id+"F0.wireOp",EDGE,"E7.4.14.0"),sQuery(id+"F0.wireOp",EDGE,"E7.8.14.0"),sQuery(id+"F0.wireOp",EDGE,"E7.11.14.0"),sQuery(id+"F0.wireOp",EDGE,"E7.14.14.0"),sQuery(id+"F0.wireOp",EDGE,"E7.17.14.0"),sQuery(id+"F0.wireOp",EDGE,"E7.28.14.0"),sQuery(id+"F0.wireOp",EDGE,"E7.31.14.0"),sQuery(id+"F0.wireOp",EDGE,"E7.34.14.0"),sQuery(id+"F0.wireOp",EDGE,"E7.37.14.0"),sQuery(id+"F0.wireOp",EDGE,"E7.1.15.0"),sQuery(id+"F0.wireOp",EDGE,"E7.4.15.0"),sQuery(id+"F0.wireOp",EDGE,"E7.8.15.0"),sQuery(id+"F0.wireOp",EDGE,"E7.11.15.0"),sQuery(id+"F0.wireOp",EDGE,"E7.14.15.0"),sQuery(id+"F0.wireOp",EDGE,"E7.17.15.0"),sQuery(id+"F0.wireOp",EDGE,"E7.28.15.0"),sQuery(id+"F0.wireOp",EDGE,"E7.31.15.0"),sQuery(id+"F0.wireOp",EDGE,"E7.34.15.0"),sQuery(id+"F0.wireOp",EDGE,"E7.37.15.0")])]});
            hole(context, id + "F2", {"style" : HoleStyle.SIMPLE, "endStyle" : HoleEndStyle.THROUGH, "oppositeDirection" : true, "standardTappedOrClearance" : lookupTablePath({ "fit" : "Normal (ASME)", "standard" : "ANSI", "size" : "1/2", "type" : "Clearance" }), "standardBlindInLast" : lookupTablePath({ "fit" : "Free", "standard" : "ANSI", "size" : "1/2", "type" : "Clearance" }), "holeDiameter" : 13.5 * mm, "majorDiameter" : 5 * mm, "isTappedThrough" : true, "tappedDepth" : 12.7 * mm, "tapClearance" : 3, "locations" : qUnion([Q0]), "scope" : qUnion([Q1])});
        }
        {
            var Q0;
            {var subQ3=sQuery(id+"F0.wireOp",EDGE,"E12");Q0=makeQuery(id+"F0.imprint","IMPRINT",FACE,{"disambiguationData":[TD([[makeQuery(id+"F0.imprint","IMPRINT",EDGE,{"derivedFrom":subQ3}),-1.0]])]});}
            extrude(context, id + "F3", {"entities" : qUnion([Q0]), "operationType" : NewBodyOperationType.ADD, "depth" : .75 * mm, "offsetDistance" : 25 * mm});
        }
        {
            var Q0;
            Q0=makeQuery(id+"F1.opExtrude","SWEPT_BODY",BODY,{"disambiguationData":[OSD([sQuery(id+"F0.wireOp",EDGE,"E0.bottom"),sQuery(id+"F0.wireOp",EDGE,"E0.top"),sQuery(id+"F0.wireOp",EDGE,"E0.left"),sQuery(id+"F0.wireOp",EDGE,"E0.right"),sQuery(id+"F0.wireOp",EDGE,"E3.bottom"),sQuery(id+"F0.wireOp",EDGE,"E3.top"),sQuery(id+"F0.wireOp",EDGE,"E4.bottom"),sQuery(id+"F0.wireOp",EDGE,"E4.top"),sQuery(id+"F0.wireOp",EDGE,"E4.left"),sQuery(id+"F0.wireOp",EDGE,"E4.right"),sQuery(id+"F0.wireOp",EDGE,"E5.bottom"),sQuery(id+"F0.wireOp",EDGE,"E5.top"),sQuery(id+"F0.wireOp",EDGE,"E5.left"),sQuery(id+"F0.wireOp",EDGE,"E5.right"),sQuery(id+"F0.wireOp",EDGE,"E6.1.0.1"),sQuery(id+"F0.wireOp",EDGE,"E6.1.0.2"),sQuery(id+"F0.wireOp",EDGE,"E6.1.0.4"),sQuery(id+"F0.wireOp",EDGE,"E6.1.0.5"),sQuery(id+"F0.wireOp",EDGE,"E6.1.0.6"),sQuery(id+"F0.wireOp",EDGE,"E6.1.0.7"),sQuery(id+"F0.wireOp",EDGE,"E6.1.0.12"),sQuery(id+"F0.wireOp",EDGE,"E6.1.0.13"),sQuery(id+"F0.wireOp",EDGE,"E6.1.0.14"),sQuery(id+"F0.wireOp",EDGE,"E6.1.0.15"),sQuery(id+"F0.wireOp",EDGE,"E6.2.0.1"),sQuery(id+"F0.wireOp",EDGE,"E6.2.0.2"),sQuery(id+"F0.wireOp",EDGE,"E6.2.0.4"),sQuery(id+"F0.wireOp",EDGE,"E6.2.0.5"),sQuery(id+"F0.wireOp",EDGE,"E6.2.0.6"),sQuery(id+"F0.wireOp",EDGE,"E6.2.0.7"),sQuery(id+"F0.wireOp",EDGE,"E6.2.0.12"),sQuery(id+"F0.wireOp",EDGE,"E6.2.0.13"),sQuery(id+"F0.wireOp",EDGE,"E6.2.0.14"),sQuery(id+"F0.wireOp",EDGE,"E6.2.0.15"),sQuery(id+"F0.wireOp",EDGE,"E6.3.0.1"),sQuery(id+"F0.wireOp",EDGE,"E6.3.0.2"),sQuery(id+"F0.wireOp",EDGE,"E6.3.0.4"),sQuery(id+"F0.wireOp",EDGE,"E6.3.0.5"),sQuery(id+"F0.wireOp",EDGE,"E6.3.0.6"),sQuery(id+"F0.wireOp",EDGE,"E6.3.0.7"),sQuery(id+"F0.wireOp",EDGE,"E6.3.0.12"),sQuery(id+"F0.wireOp",EDGE,"E6.3.0.13"),sQuery(id+"F0.wireOp",EDGE,"E6.3.0.14"),sQuery(id+"F0.wireOp",EDGE,"E6.3.0.15"),sQuery(id+"F0.wireOp",EDGE,"E6.4.0.1"),sQuery(id+"F0.wireOp",EDGE,"E6.4.0.2"),sQuery(id+"F0.wireOp",EDGE,"E6.4.0.4"),sQuery(id+"F0.wireOp",EDGE,"E6.4.0.5"),sQuery(id+"F0.wireOp",EDGE,"E6.4.0.6"),sQuery(id+"F0.wireOp",EDGE,"E6.4.0.7"),sQuery(id+"F0.wireOp",EDGE,"E6.4.0.12"),sQuery(id+"F0.wireOp",EDGE,"E6.4.0.13"),sQuery(id+"F0.wireOp",EDGE,"E6.4.0.14"),sQuery(id+"F0.wireOp",EDGE,"E6.4.0.15"),sQuery(id+"F0.wireOp",EDGE,"E6.5.0.1"),sQuery(id+"F0.wireOp",EDGE,"E6.5.0.2"),sQuery(id+"F0.wireOp",EDGE,"E6.5.0.4"),sQuery(id+"F0.wireOp",EDGE,"E6.5.0.5"),sQuery(id+"F0.wireOp",EDGE,"E6.5.0.6"),sQuery(id+"F0.wireOp",EDGE,"E6.5.0.7"),sQuery(id+"F0.wireOp",EDGE,"E6.5.0.12"),sQuery(id+"F0.wireOp",EDGE,"E6.5.0.13"),sQuery(id+"F0.wireOp",EDGE,"E6.5.0.14"),sQuery(id+"F0.wireOp",EDGE,"E6.5.0.15"),sQuery(id+"F0.wireOp",EDGE,"E6.6.0.1"),sQuery(id+"F0.wireOp",EDGE,"E6.6.0.2"),sQuery(id+"F0.wireOp",EDGE,"E6.6.0.4"),sQuery(id+"F0.wireOp",EDGE,"E6.6.0.5"),sQuery(id+"F0.wireOp",EDGE,"E6.6.0.6"),sQuery(id+"F0.wireOp",EDGE,"E6.6.0.7"),sQuery(id+"F0.wireOp",EDGE,"E6.6.0.12"),sQuery(id+"F0.wireOp",EDGE,"E6.6.0.13"),sQuery(id+"F0.wireOp",EDGE,"E6.6.0.14"),sQuery(id+"F0.wireOp",EDGE,"E6.6.0.15"),sQuery(id+"F0.wireOp",EDGE,"E6.7.0.1"),sQuery(id+"F0.wireOp",EDGE,"E6.7.0.2"),sQuery(id+"F0.wireOp",EDGE,"E6.7.0.4"),sQuery(id+"F0.wireOp",EDGE,"E6.7.0.5"),sQuery(id+"F0.wireOp",EDGE,"E6.7.0.6"),sQuery(id+"F0.wireOp",EDGE,"E6.7.0.7"),sQuery(id+"F0.wireOp",EDGE,"E6.7.0.12"),sQuery(id+"F0.wireOp",EDGE,"E6.7.0.13"),sQuery(id+"F0.wireOp",EDGE,"E6.7.0.14"),sQuery(id+"F0.wireOp",EDGE,"E6.7.0.15"),sQuery(id+"F0.wireOp",EDGE,"E6.8.0.1"),sQuery(id+"F0.wireOp",EDGE,"E6.8.0.2"),sQuery(id+"F0.wireOp",EDGE,"E6.8.0.4"),sQuery(id+"F0.wireOp",EDGE,"E6.8.0.5"),sQuery(id+"F0.wireOp",EDGE,"E6.8.0.6"),sQuery(id+"F0.wireOp",EDGE,"E6.8.0.7"),sQuery(id+"F0.wireOp",EDGE,"E6.8.0.12"),sQuery(id+"F0.wireOp",EDGE,"E6.8.0.13"),sQuery(id+"F0.wireOp",EDGE,"E6.8.0.14"),sQuery(id+"F0.wireOp",EDGE,"E6.8.0.15"),sQuery(id+"F0.wireOp",EDGE,"E6.9.0.1"),sQuery(id+"F0.wireOp",EDGE,"E6.9.0.2"),sQuery(id+"F0.wireOp",EDGE,"E6.9.0.4"),sQuery(id+"F0.wireOp",EDGE,"E6.9.0.5"),sQuery(id+"F0.wireOp",EDGE,"E6.9.0.6"),sQuery(id+"F0.wireOp",EDGE,"E6.9.0.7"),sQuery(id+"F0.wireOp",EDGE,"E6.9.0.12"),sQuery(id+"F0.wireOp",EDGE,"E6.9.0.13"),sQuery(id+"F0.wireOp",EDGE,"E6.9.0.14"),sQuery(id+"F0.wireOp",EDGE,"E6.9.0.15"),sQuery(id+"F0.wireOp",EDGE,"E6.10.0.1"),sQuery(id+"F0.wireOp",EDGE,"E6.10.0.2"),sQuery(id+"F0.wireOp",EDGE,"E6.10.0.4"),sQuery(id+"F0.wireOp",EDGE,"E6.10.0.5"),sQuery(id+"F0.wireOp",EDGE,"E6.10.0.6"),sQuery(id+"F0.wireOp",EDGE,"E6.10.0.7"),sQuery(id+"F0.wireOp",EDGE,"E6.10.0.12"),sQuery(id+"F0.wireOp",EDGE,"E6.10.0.13"),sQuery(id+"F0.wireOp",EDGE,"E6.10.0.14"),sQuery(id+"F0.wireOp",EDGE,"E6.10.0.15"),sQuery(id+"F0.wireOp",EDGE,"E6.11.0.1"),sQuery(id+"F0.wireOp",EDGE,"E6.11.0.2"),sQuery(id+"F0.wireOp",EDGE,"E6.11.0.4"),sQuery(id+"F0.wireOp",EDGE,"E6.11.0.5"),sQuery(id+"F0.wireOp",EDGE,"E6.11.0.6"),sQuery(id+"F0.wireOp",EDGE,"E6.11.0.7"),sQuery(id+"F0.wireOp",EDGE,"E6.11.0.12"),sQuery(id+"F0.wireOp",EDGE,"E6.11.0.13"),sQuery(id+"F0.wireOp",EDGE,"E6.11.0.14"),sQuery(id+"F0.wireOp",EDGE,"E6.11.0.15"),sQuery(id+"F0.wireOp",EDGE,"E6.12.0.1"),sQuery(id+"F0.wireOp",EDGE,"E6.12.0.2"),sQuery(id+"F0.wireOp",EDGE,"E6.12.0.4"),sQuery(id+"F0.wireOp",EDGE,"E6.12.0.5"),sQuery(id+"F0.wireOp",EDGE,"E6.12.0.6"),sQuery(id+"F0.wireOp",EDGE,"E6.12.0.7"),sQuery(id+"F0.wireOp",EDGE,"E6.12.0.12"),sQuery(id+"F0.wireOp",EDGE,"E6.12.0.13"),sQuery(id+"F0.wireOp",EDGE,"E6.12.0.14"),sQuery(id+"F0.wireOp",EDGE,"E6.12.0.15"),sQuery(id+"F0.wireOp",EDGE,"E6.13.0.1"),sQuery(id+"F0.wireOp",EDGE,"E6.13.0.2"),sQuery(id+"F0.wireOp",EDGE,"E6.13.0.4"),sQuery(id+"F0.wireOp",EDGE,"E6.13.0.5"),sQuery(id+"F0.wireOp",EDGE,"E6.13.0.6"),sQuery(id+"F0.wireOp",EDGE,"E6.13.0.7"),sQuery(id+"F0.wireOp",EDGE,"E6.13.0.12"),sQuery(id+"F0.wireOp",EDGE,"E6.13.0.13"),sQuery(id+"F0.wireOp",EDGE,"E6.13.0.14"),sQuery(id+"F0.wireOp",EDGE,"E6.13.0.15"),sQuery(id+"F0.wireOp",EDGE,"E7.1.14.0"),sQuery(id+"F0.wireOp",EDGE,"E7.4.14.0"),sQuery(id+"F0.wireOp",EDGE,"E7.8.14.0"),sQuery(id+"F0.wireOp",EDGE,"E7.11.14.0"),sQuery(id+"F0.wireOp",EDGE,"E7.14.14.0"),sQuery(id+"F0.wireOp",EDGE,"E7.17.14.0"),sQuery(id+"F0.wireOp",EDGE,"E7.28.14.0"),sQuery(id+"F0.wireOp",EDGE,"E7.31.14.0"),sQuery(id+"F0.wireOp",EDGE,"E7.34.14.0"),sQuery(id+"F0.wireOp",EDGE,"E7.37.14.0"),sQuery(id+"F0.wireOp",EDGE,"E7.1.15.0"),sQuery(id+"F0.wireOp",EDGE,"E7.4.15.0"),sQuery(id+"F0.wireOp",EDGE,"E7.8.15.0"),sQuery(id+"F0.wireOp",EDGE,"E7.11.15.0"),sQuery(id+"F0.wireOp",EDGE,"E7.14.15.0"),sQuery(id+"F0.wireOp",EDGE,"E7.17.15.0"),sQuery(id+"F0.wireOp",EDGE,"E7.28.15.0"),sQuery(id+"F0.wireOp",EDGE,"E7.31.15.0"),sQuery(id+"F0.wireOp",EDGE,"E7.34.15.0"),sQuery(id+"F0.wireOp",EDGE,"E7.37.15.0"),sQuery(id+"F0.wireOp",EDGE,"E11.left")])]});
            var Q1;
            Q1=sQuery(id+"F0.wireOp",VERTEX,"E6.9.0.0");
            transform(context, id + "F4", {"entities" : qUnion([Q0]), "transformType" : TransformType.SCALE_UNIFORMLY, "scale" : 1.05, "scalePoint" : qUnion([Q1]), "makeCopy" : false});
        }
    });
